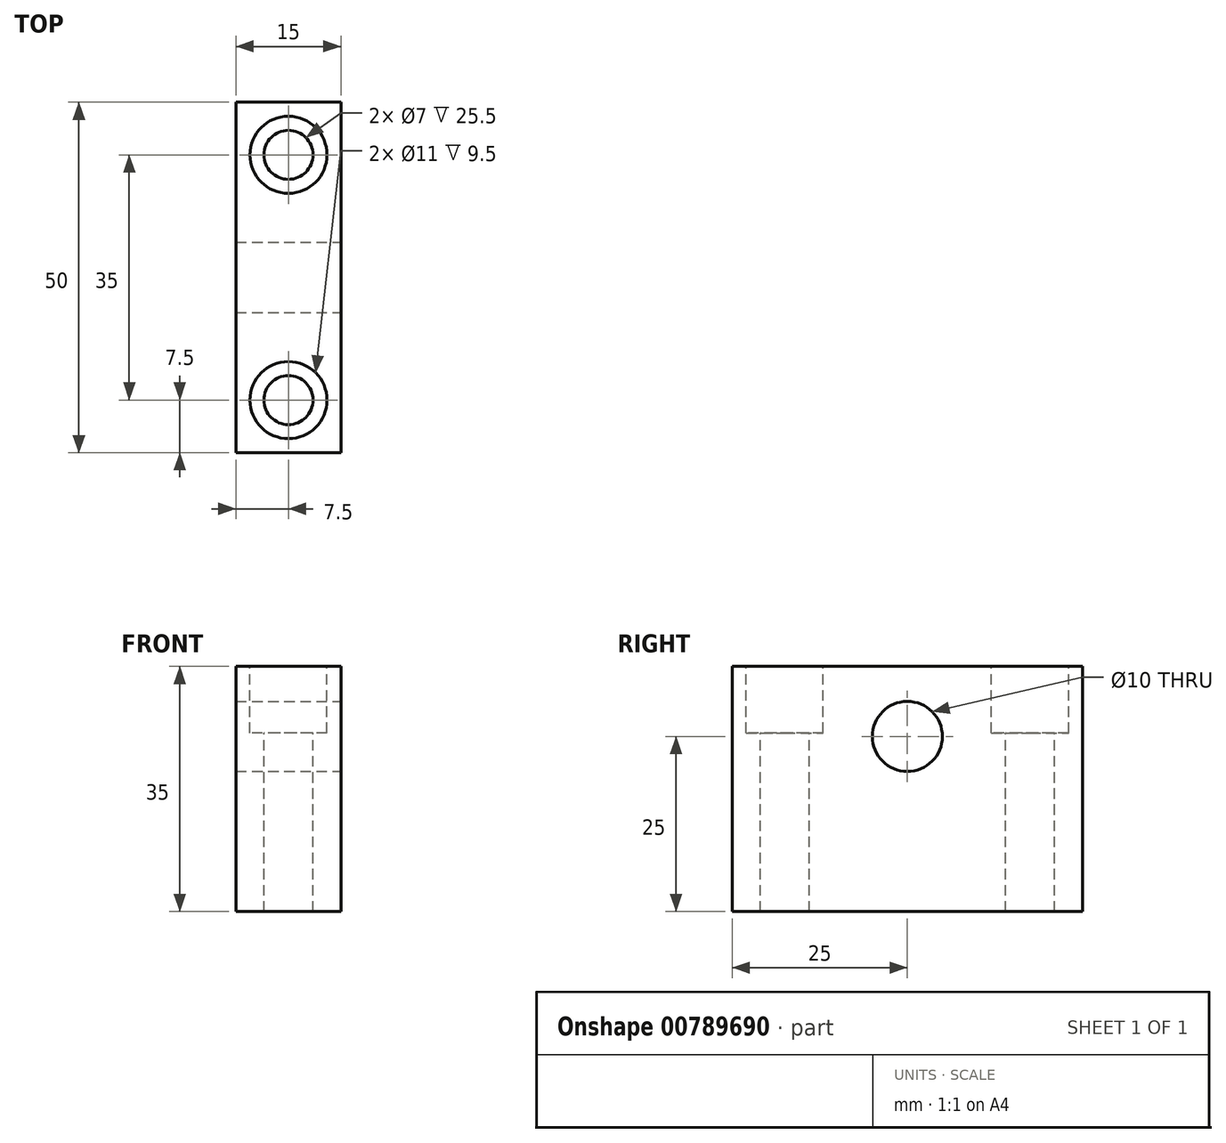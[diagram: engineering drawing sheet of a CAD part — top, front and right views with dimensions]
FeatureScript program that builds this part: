
annotation { "Feature Type Name" : "Feature", "Feature Type Description" : "" }
export const myFeature = defineFeature(function(context is Context, id is Id, definition is map)
    precondition{}
    {
        {
            var Q0;
            Q0=qCreatedBy(makeId("Top.planeOp"),FACE);
            var sketch = newSketch(context, id + "F0", { "sketchPlane" : qUnion([Q0])});
            skLineSegment(sketch, "E0.bottom", {"start": v(7.5, -25) * mm, "end": v(-7.5, -25) * mm});
            skLineSegment(sketch, "E0.top", {"start": v(7.5, 25) * mm, "end": v(-7.5, 25) * mm});
            skLineSegment(sketch, "E0.left", {"start": v(7.5, -25) * mm, "end": v(7.5, 25) * mm});
            skLineSegment(sketch, "E0.right", {"start": v(-7.5, -25) * mm, "end": v(-7.5, 25) * mm});
            skPoint(sketch, "E0.middle", {"position": v(0, 0) * mm});
            skSolve(sketch);
        }
        {
            var Q0;
            Q0 = qSketchRegion(id + "F0", true);
            extrude(context, id + "F1", {"entities" : qUnion([Q0]), "depth" : 35 * mm, "offsetDistance" : 25 * mm});
        }
        {
            var Q0;
            Q0=makeQuery(id+"F1.opExtrude","SWEPT_FACE",FACE,{"disambiguationData":[OSD([sQuery(id+"F0.wireOp",EDGE,"E0.left")])]});
            var sketch = newSketch(context, id + "F2", { "sketchPlane" : qUnion([Q0])});
            skCircle(sketch, "E1", {"center": v(0, 25) * mm, "radius": 5 * mm});
            skSolve(sketch);
        }
        {
            var Q0;
            Q0 = qSketchRegion(id + "F2", true);
            extrude(context, id + "F3", {"entities" : qUnion([Q0]), "operationType" : NewBodyOperationType.REMOVE, "endBound" : BoundingType.UP_TO_NEXT, "oppositeDirection" : true, "depth" : 25 * mm, "offsetDistance" : 25 * mm});
        }
        {
            var Q0;
            Q0=makeQuery(id+"F1.opExtrude","CAP_FACE",FACE,{"disambiguationData":[OSD([sQuery(id+"F0.wireOp",EDGE,"E0.bottom"),sQuery(id+"F0.wireOp",EDGE,"E0.top"),sQuery(id+"F0.wireOp",EDGE,"E0.left"),sQuery(id+"F0.wireOp",EDGE,"E0.right")])],"isStart":false});
            var sketch = newSketch(context, id + "F4", { "sketchPlane" : qUnion([Q0])});
            skCircle(sketch, "E2", {"center": v(0, -17.5) * mm, "radius": 3.5 * mm});
            skCircle(sketch, "E3.MirrorC", {"center": v(0, 17.5) * mm, "radius": 3.5 * mm});
            skSolve(sketch);
        }
        {
            var Q0;
            Q0 = qSketchRegion(id + "F4", true);
            extrude(context, id + "F5", {"entities" : qUnion([Q0]), "operationType" : NewBodyOperationType.REMOVE, "endBound" : BoundingType.UP_TO_NEXT, "oppositeDirection" : true, "depth" : 25 * mm, "offsetDistance" : 25 * mm});
        }
        {
            var Q0;
            Q0=makeQuery(id+"F1.opExtrude","CAP_FACE",FACE,{"disambiguationData":[OSD([sQuery(id+"F0.wireOp",EDGE,"E0.bottom"),sQuery(id+"F0.wireOp",EDGE,"E0.top"),sQuery(id+"F0.wireOp",EDGE,"E0.left"),sQuery(id+"F0.wireOp",EDGE,"E0.right")])],"isStart":false});
            var sketch = newSketch(context, id + "F6", { "sketchPlane" : qUnion([Q0])});
            skCircle(sketch, "E4", {"center": v(0, -17.5) * mm, "radius": 5.5 * mm});
            skCircle(sketch, "E5", {"center": v(0, 17.5) * mm, "radius": 5.5 * mm});
            skSolve(sketch);
        }
        {
            var Q0;
            Q0 = qSketchRegion(id + "F6", true);
            extrude(context, id + "F7", {"entities" : qUnion([Q0]), "operationType" : NewBodyOperationType.REMOVE, "oppositeDirection" : true, "depth" : 9.5 * mm, "offsetDistance" : 25 * mm});
        }
    });
